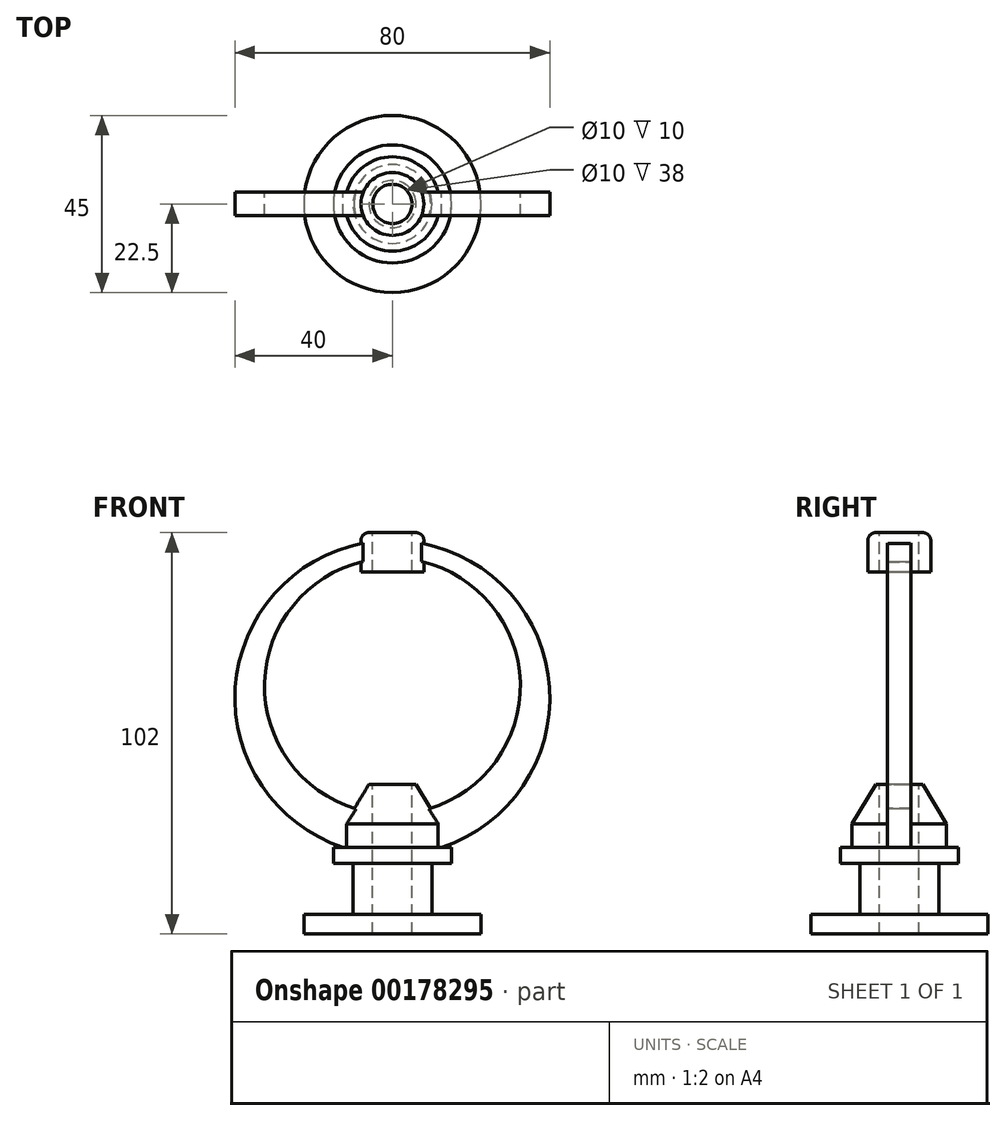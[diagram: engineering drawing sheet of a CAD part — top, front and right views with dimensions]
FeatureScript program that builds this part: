
annotation { "Feature Type Name" : "Feature", "Feature Type Description" : "" }
export const myFeature = defineFeature(function(context is Context, id is Id, definition is map)
    precondition{}
    {
        {
            var Q0;
            Q0=qCreatedBy(makeId("Front.planeOp"),FACE);
            var sketch = newSketch(context, id + "F0", { "sketchPlane" : qUnion([Q0])});
            skLineSegment(sketch, "E0", {"start": v(0, -25.67) * mm, "end": v(0, 83.17) * mm, "construction": true});
            skLineSegment(sketch, "E1", {"start": v(0, 0) * mm, "end": v(22.5, 0) * mm});
            skLineSegment(sketch, "E2", {"start": v(22.5, 0) * mm, "end": v(22.5, 5) * mm});
            skLineSegment(sketch, "E3", {"start": v(22.5, 5) * mm, "end": v(10, 5) * mm});
            skLineSegment(sketch, "E4", {"start": v(10, 5) * mm, "end": v(10, 18) * mm});
            skLineSegment(sketch, "E5", {"start": v(10, 18) * mm, "end": v(15, 18) * mm});
            skLineSegment(sketch, "E6", {"start": v(15, 18) * mm, "end": v(15, 22) * mm});
            skLineSegment(sketch, "E7", {"start": v(15, 22) * mm, "end": v(12, 22) * mm});
            skLineSegment(sketch, "E8", {"start": v(12, 22) * mm, "end": v(12, 28) * mm});
            skLineSegment(sketch, "E9", {"start": v(12, 28) * mm, "end": v(6, 38) * mm});
            skLineSegment(sketch, "E10", {"start": v(6, 38) * mm, "end": v(0, 38) * mm});
            skLineSegment(sketch, "E11", {"start": v(0, 38) * mm, "end": v(0, 0) * mm});
            skSolve(sketch);
        }
        {
            var Q0;
            Q0=qSketchRegion(id+"F0",true);
            var Q1;
            Q1=sQuery(id+"F0.wireOp",EDGE,"E0");
            revolve(context, id + "F1", {"entities" : qUnion([Q0]), "axis" : qUnion([Q1]), "revolveType" : RevolveType.FULL});
        }
        {
            var Q0;
            Q0=qCreatedBy(makeId("Front.planeOp"),FACE);
            var sketch = newSketch(context, id + "F2", { "sketchPlane" : qUnion([Q0])});
            skCircle(sketch, "E12", {"center": v(0, 60) * mm, "radius": 40 * mm});
            skCircle(sketch, "E13", {"center": v(0, 63) * mm, "radius": 32.5 * mm});
            skSolve(sketch);
        }
        {
            var Q0;
            Q0=qSketchRegion(id+"F2",true);
            extrude(context, id + "F3", {"entities" : qUnion([Q0]), "operationType" : NewBodyOperationType.ADD, "depth" : 6 * mm, "symmetric" : true});
        }
        {
            var Q0;
            Q0=qCreatedBy(makeId("Front.planeOp"),FACE);
            var sketch = newSketch(context, id + "F4", { "sketchPlane" : qUnion([Q0])});
            skLineSegment(sketch, "E14", {"start": v(0, 104.1) * mm, "end": v(0, 84.9) * mm, "construction": true});
            skLineSegment(sketch, "E15.bottom", {"start": v(0, 102) * mm, "end": v(8, 102) * mm});
            skLineSegment(sketch, "E15.top", {"start": v(0, 92) * mm, "end": v(8, 92) * mm});
            skLineSegment(sketch, "E15.left", {"start": v(0, 102) * mm, "end": v(0, 92) * mm});
            skLineSegment(sketch, "E15.right", {"start": v(8, 102) * mm, "end": v(8, 92) * mm});
            skSolve(sketch);
        }
        {
            var Q0;
            Q0=qSketchRegion(id+"F4",true);
            var Q1;
            Q1=sQuery(id+"F4.wireOp",EDGE,"E14");
            revolve(context, id + "F5", {"operationType" : NewBodyOperationType.ADD, "entities" : qUnion([Q0]), "axis" : qUnion([Q1]), "revolveType" : RevolveType.FULL});
        }
        {
            var Q0;
            Q0=makeQuery(id+"F5.opRevolve","SWEPT_FACE",FACE,{"disambiguationData":[OSD([sQuery(id+"F4.wireOp",EDGE,"E15.bottom")])]});
            var sketch = newSketch(context, id + "F6", { "sketchPlane" : qUnion([Q0])});
            skCircle(sketch, "E16", {"center": v(0, 0) * mm, "radius": 5 * mm});
            skSolve(sketch);
        }
        {
            var Q0;
            Q0=qSketchRegion(id+"F6",true);
            extrude(context, id + "F7", {"entities" : qUnion([Q0]), "operationType" : NewBodyOperationType.REMOVE, "endBound" : BoundingType.THROUGH_ALL, "oppositeDirection" : true, "depth" : 25 * mm});
        }
        {
            var Q0;
            Q0=makeQuery(id+"F5.opRevolve","SWEPT_EDGE",EDGE,{"disambiguationData":[OSD([sQuery(id+"F4.wireOp",EDGE,"E15.bottom"),sQuery(id+"F4.wireOp",EDGE,"E15.right")])]});
            fillet(context, id + "F8", {"entities" : qUnion([Q0]), "radius" : 2 * mm, "tangentPropagation" : true, "allowEdgeOverflow" : false});
        }
    });
